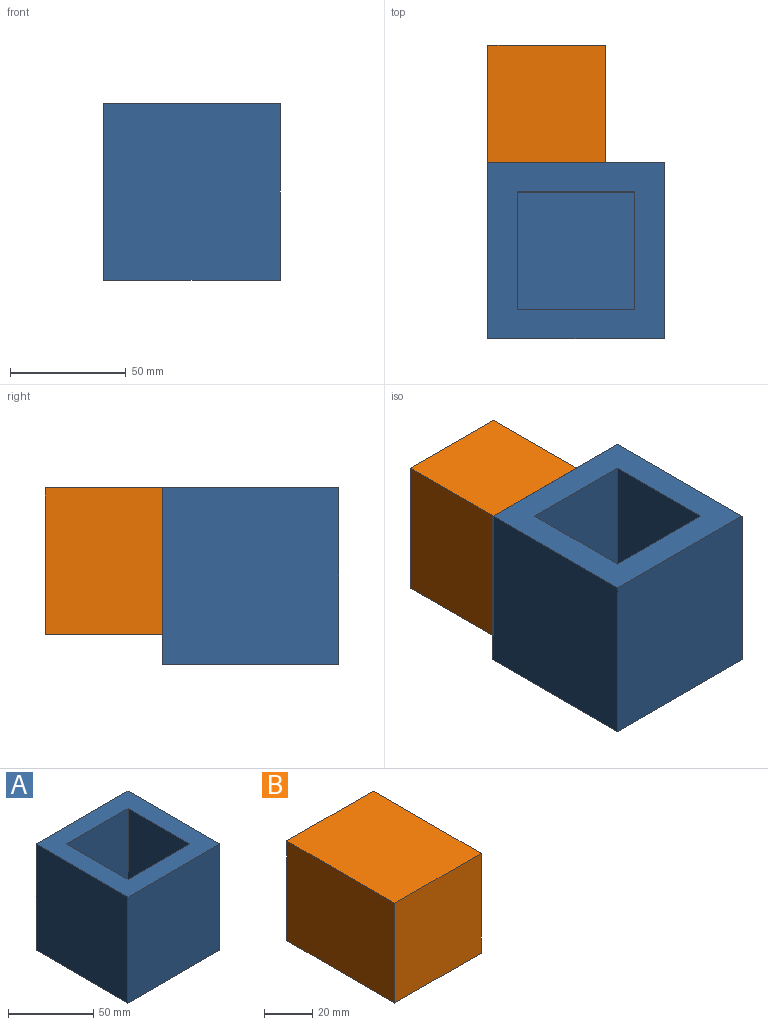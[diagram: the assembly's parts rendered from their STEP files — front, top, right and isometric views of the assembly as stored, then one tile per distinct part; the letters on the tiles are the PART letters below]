
ASSEMBLY  parts=2 mates=1
PART A: 11 faces, bbox 76.2x76.2x76.2 mm
  f0: plane 76.2x76.2mm, normal (0,0,1), area 3225.8mm2, adj f1,f3,f4,f5,f6,f8,f9,f10
  f1: plane 76.2x76.2mm, normal (0,-1,0), area 5806.4mm2, adj f0,f2,f4,f5
  f2: plane 76.2x76.2mm, normal (0,0,-1), area 5806.4mm2, adj f1,f3,f4,f5
  f3: plane 76.2x76.2mm, normal (0,1,0), area 5806.4mm2, adj f0,f2,f4,f5
  f4: plane 76.2x76.2mm, normal (1,0,0), area 5806.4mm2, adj f0,f1,f2,f3
  f5: plane 76.2x76.2mm, normal (-1,0,0), area 5806.4mm2, adj f0,f1,f2,f3
  f6: plane 63.5x50.8mm, normal (0,1,0), area 3225.8mm2, adj f0,f7,f9,f10
  f7: plane 50.8x50.8mm, normal (0,0,1), area 2580.6mm2, adj f6,f8,f9,f10
  f8: plane 63.5x50.8mm, normal (0,-1,0), area 3225.8mm2, adj f0,f7,f9,f10
  f9: plane 63.5x50.8mm, normal (-1,0,0), area 3225.8mm2, adj f0,f6,f7,f8
  f10: plane 63.5x50.8mm, normal (1,0,0), area 3225.8mm2, adj f0,f6,f7,f8
PART B: 6 faces, bbox 50.8x63.5x50.8 mm
  f0: plane 63.5x50.8mm, normal (0,0,1), area 3225.8mm2, adj f1,f3,f4,f5
  f1: plane 63.5x50.8mm, normal (-1,0,0), area 3225.8mm2, adj f0,f2,f4,f5
  f2: plane 63.5x50.8mm, normal (0,0,-1), area 3225.8mm2, adj f1,f3,f4,f5
  f3: plane 63.5x50.8mm, normal (1,0,0), area 3225.8mm2, adj f0,f2,f4,f5
  f4: plane 50.8x50.8mm, normal (0,-1,0), area 2580.6mm2, adj f0,f1,f2,f3
  f5: plane 50.8x50.8mm, normal (0,1,0), area 2580.6mm2, adj f0,f1,f2,f3
PLACE A t=(2.25,-76.24,-0.03)mm fixed
PLACE B rot(axis=(1,0,0),90deg) t=(2.25,50.76,76.17)mm
MATE fastened B.f5 <-> A.f0  axis (0,0,1) through (2.25,-0.04,76.17)mm
